# Revit family: Wireless_Ceiling_Sensor-Lutron-Radio_Powr_Savr-LRF2--
name_source: partatom
category: Lighting Devices
revit_build: Autodesk Revit 2015 (Build: 20160512_0715(x64)
units: mm (PartAtom-declared; Revit-internal decimal feet)

## types (1)
- ERROR_LOAD Type Catalog
    Assembly Code = D5030800
    Ceiling Opening Diameter = 0' - 3"
    Ceiling Opening Radius = 0' - 1 1/2"
    Current = 14 mA
    Default Elevation = 0' - 0"
    Description = Wireless Ceiling Mount Sensor
    ENGworks URL = http://www.ENGworks.com
    Field of View = 360.00°
    Frequency = 434 MHz
    Label = OS
    Light Level = 1 fc
    Manufacturer = Lutron Electronics
    Maximum Ceiling Height = 12' - 0"
    Maximum Coverage = 676.00 SF
    Maximum Operating Temperature = 104 °F
    Maximum Room Coverage (L x W) = 12ft x 12ft
    Minimum Ceiling Height = 8' - 0"
    Minimum Clearance = 4' - 0"
    Minimum Coverage = 324.00 SF
    Minimum Operating Temperature = 32 °F
    Minimum Room Coverage (L x W) = 8ft x 8ft
    Model = LRF2-OCR2B-P-WH
    Mounting Diameter = 0' - 2 27/32"
    Mounting Radius = 0' - 1 7/16"
    Overall Depth = 0' - 3 9/16"
    Overall Width = 0' - 1 1/8"
    Product Page URL = http://www.lutron.com
    Radius of Coverage at Floor = 13' - 0"
    Sensor Body Height = 0' - 0 1/2"
    Sensor Cover Offset = 0' - 0 7/8"
    Sensor Diameter = 0' - 1 1/2"
    Sensor Material = Plastic - Lutron - White
    Sensor Radius = 0' - 0 3/4"
    Series = Radio Powr Savr
    Standards = FCC certified; IC certified; COFETEL certified; RoHS compliant
    Thomas Enterprise Solutions URL = http://www.thomasenterprisesolutions.com
    URL = http://www.lutron.com
    Version = 1
    Voltage = 3 V

## geometry (parser evidence)
native form markers: Blend x13, Sweep x3
no freeform markers — native parametric forms only
